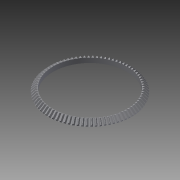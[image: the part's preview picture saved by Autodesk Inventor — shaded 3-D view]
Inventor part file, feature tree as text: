
AUTODESK INVENTOR PART (.ipt)
format: ipt  version: 2015 (Build 190159000, 159)  size: 1,231,360 bytes
history: native  units: in
note: dims shown in document units (in); Inventor stores cm internally (conversion verified against a paired STEP export)
features: extrude x4, sketch x4, pattern_circular x1
ambient origin geometry x8: Origin, YZ Plane, XZ Plane, XY Plane, X Axis, Y Axis, Z Axis, Center Point
bodies: Body1 (feature_tree)
feature tree (9):
  extrude  "Extrusion7"  Depth=6.75in
  extrude  "Extrusion8"  Depth=0.75in TaperAngle=0.0deg
  extrude  "Extrusion9"  Depth=0.25in
  extrude  "Extrusion10"  [1 undecoded]
  pattern_circular  "Circular Pattern3"  [2 undecoded]
  sketch  "Sketch8"  dims[d25=6.75in d26=0.75in d27=-0.3092in]
  sketch  "Sketch9"  dims[d28=12.0in d29=0.75in d30=0.0in]
  sketch  "Sketch12"  dims[d33=0.25in d34=-0.169in d35=0.25in d36=-0.3436in]
  sketch  "Sketch13"  dims[d37=31.4961in d38=360.0deg]
note: 3 required parameter values undecoded (feature->parameter linkage not recoverable at this tier; creation-order binding heuristic only, values carry confidence <= 0.55)
